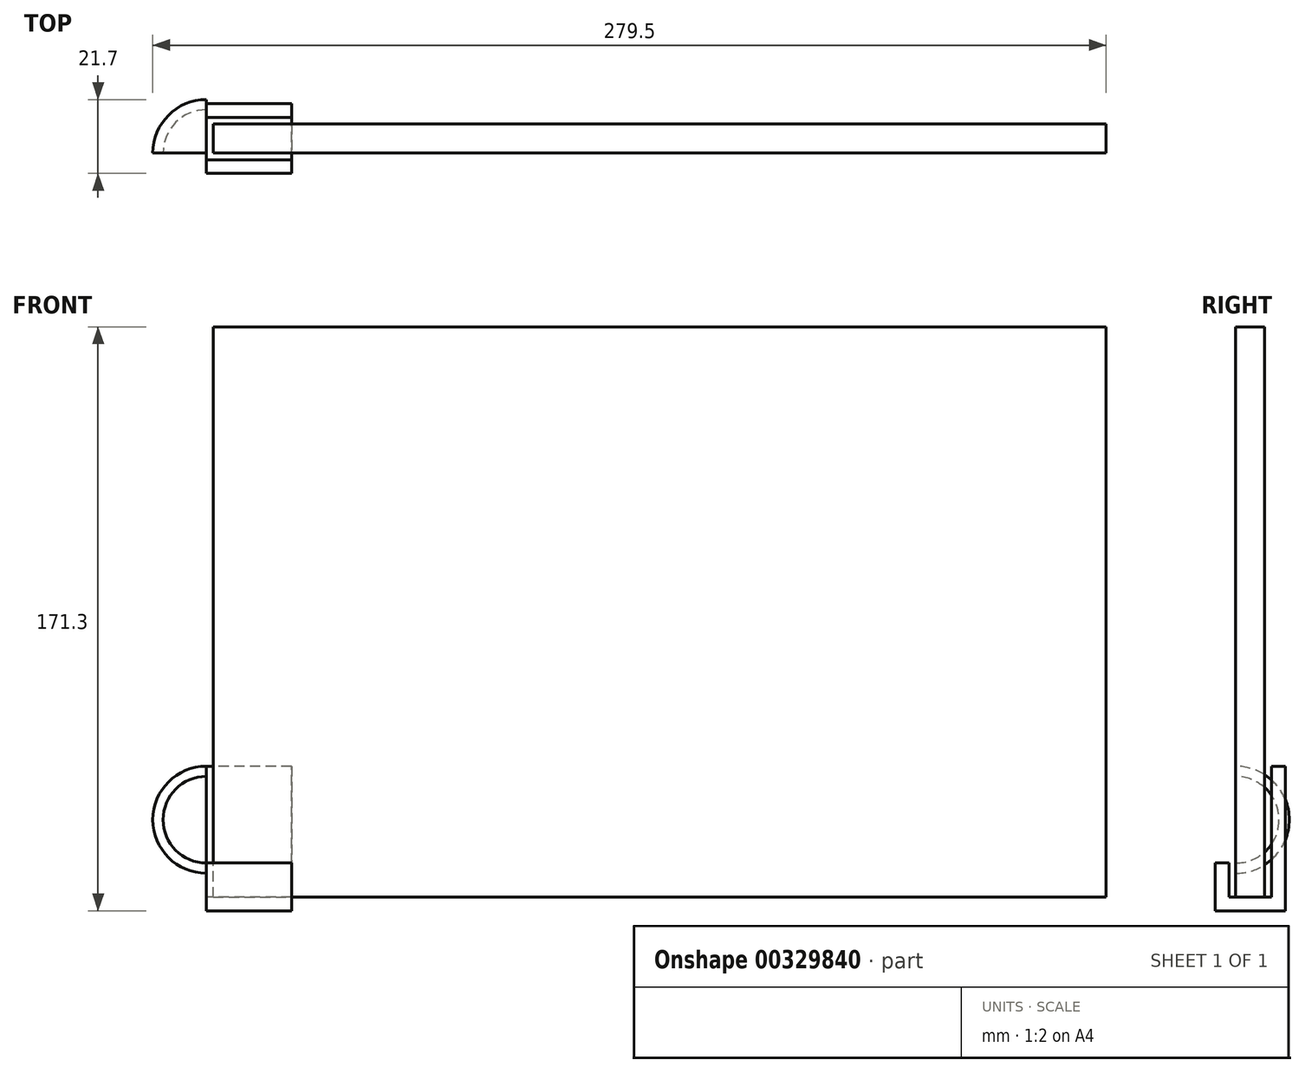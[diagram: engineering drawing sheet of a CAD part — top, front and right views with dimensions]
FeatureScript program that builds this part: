
annotation { "Feature Type Name" : "Feature", "Feature Type Description" : "" }
export const myFeature = defineFeature(function(context is Context, id is Id, definition is map)
    precondition{}
    {
        {
            var Q0;
            Q0=qCreatedBy(makeId("Front.planeOp"),FACE);
            var sketch = newSketch(context, id + "F0", { "sketchPlane" : qUnion([Q0])});
            skLineSegment(sketch, "E0.bottom", {"start": v(0, 0) * mm, "end": v(261.8, 0) * mm});
            skLineSegment(sketch, "E0.top", {"start": v(0, 167.3) * mm, "end": v(261.8, 167.3) * mm});
            skLineSegment(sketch, "E0.left", {"start": v(0, 0) * mm, "end": v(0, 167.3) * mm});
            skLineSegment(sketch, "E0.right", {"start": v(261.8, 0) * mm, "end": v(261.8, 167.3) * mm});
            skSolve(sketch);
        }
        {
            var Q0;
            Q0=makeQuery(id+"F0.imprint","IMPRINT",FACE,{"disambiguationData":[TD([[makeQuery(id+"F0.imprint","IMPRINT",EDGE,{"derivedFrom":sQuery(id+"F0.wireOp",EDGE,"E0.bottom")}),1.0]])]});
            extrude(context, id + "F1", {"entities" : qUnion([Q0]), "depth" : 8.5 * mm, "offsetDistance" : 25 * mm});
        }
        {
            var Q0;
            Q0=makeQuery(id+"F1.opExtrude","CAP_FACE",FACE,{"disambiguationData":[OSD([sQuery(id+"F0.wireOp",EDGE,"E0.bottom"),sQuery(id+"F0.wireOp",EDGE,"E0.top"),sQuery(id+"F0.wireOp",EDGE,"E0.left"),sQuery(id+"F0.wireOp",EDGE,"E0.right")])],"isStart":false});
            var sketch = newSketch(context, id + "F2", { "sketchPlane" : qUnion([Q0])});
            skArc(sketch, "E1", {"start": v(-2, 38.4) * mm, "mid": v(-17.7, 22.7) * mm, "end": v(-2, 7) * mm});
            skArc(sketch, "E2", {"start": v(-2, 35.4) * mm, "mid": v(-14.7, 22.7) * mm, "end": v(-2, 10) * mm});
            skLineSegment(sketch, "E3", {"start": v(-2, 38.4) * mm, "end": v(-2, 35.4) * mm});
            skLineSegment(sketch, "E4", {"start": v(-2, 35.4) * mm, "end": v(-2, 22.7) * mm, "construction": true});
            skLineSegment(sketch, "E5", {"start": v(-2, 22.7) * mm, "end": v(-2, 10) * mm, "construction": true});
            skLineSegment(sketch, "E6", {"start": v(-2, 10) * mm, "end": v(-2, 7) * mm});
            skSolve(sketch);
        }
        {
            var Q0;
            Q0 = qSketchRegion(id + "F2", true);
            var Q1;
            Q1=sQuery(id+"F2.wireOp",EDGE,"E4");
            revolve(context, id + "F3", {"surfaceOperationType" : NewSurfaceOperationType.NEW, "entities" : qUnion([Q0]), "axis" : qUnion([Q1]), "revolveType" : RevolveType.ONE_DIRECTION, "angle" : 90 * degree});
        }
        {
            var Q0;
            Q0=makeQuery(id+"F3.opRevolve","CAP_FACE",FACE,{"disambiguationData":[OSD([sQuery(id+"F2.wireOp",EDGE,"E1"),sQuery(id+"F2.wireOp",EDGE,"E2"),sQuery(id+"F2.wireOp",EDGE,"E3"),sQuery(id+"F2.wireOp",EDGE,"E6")])],"isStart":false});
            var sketch = newSketch(context, id + "F4", { "sketchPlane" : qUnion([Q0])});
            skLineSegment(sketch, "E7", {"start": v(2, 38.4) * mm, "end": v(2, 0) * mm});
            skLineSegment(sketch, "E8", {"start": v(2, 0) * mm, "end": v(-10.5, 0) * mm});
            skLineSegment(sketch, "E9", {"start": v(-10.5, 0) * mm, "end": v(-10.5, 10) * mm});
            skLineSegment(sketch, "E10", {"start": v(-10.5, 10) * mm, "end": v(-14.5, 10) * mm});
            skLineSegment(sketch, "E11", {"start": v(-14.5, 10) * mm, "end": v(-14.5, -4) * mm});
            skLineSegment(sketch, "E12", {"start": v(-14.5, -4) * mm, "end": v(6, -4) * mm});
            skLineSegment(sketch, "E13", {"start": v(6, -4) * mm, "end": v(6, 38.4) * mm});
            skLineSegment(sketch, "E14", {"start": v(6, 38.4) * mm, "end": v(2, 38.4) * mm});
            skLineSegment(sketch, "E15", {"start": v(-10.5, 10) * mm, "end": v(-8.5, 10) * mm, "construction": true});
            skLineSegment(sketch, "E16", {"start": v(0, 10) * mm, "end": v(2, 10) * mm, "construction": true});
            skSolve(sketch);
        }
        {
            var Q0;
            Q0 = qSketchRegion(id + "F4", true);
            extrude(context, id + "F5", {"entities" : qUnion([Q0]), "operationType" : NewBodyOperationType.ADD, "depth" : 25 * mm, "offsetDistance" : 25 * mm});
        }
    });
